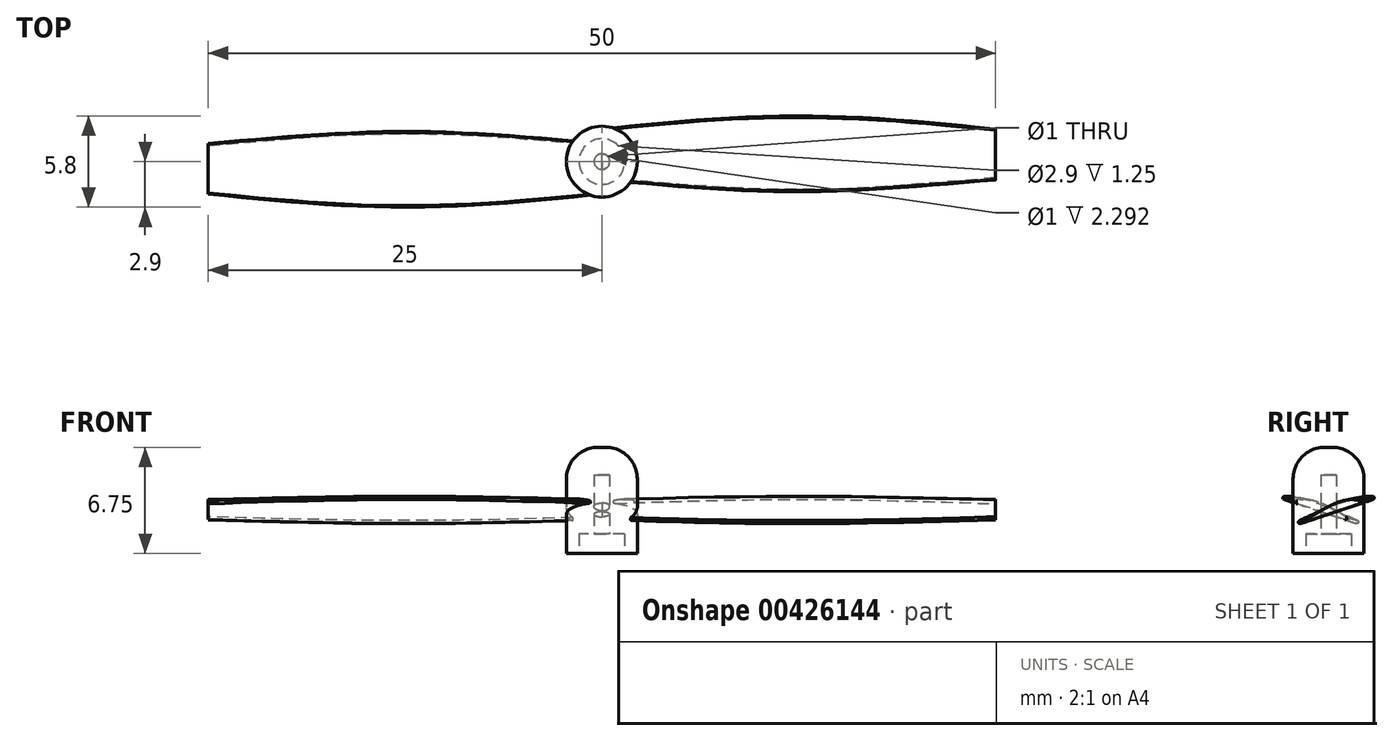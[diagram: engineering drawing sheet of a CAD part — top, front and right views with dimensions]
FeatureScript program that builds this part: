
annotation { "Feature Type Name" : "Feature", "Feature Type Description" : "" }
export const myFeature = defineFeature(function(context is Context, id is Id, definition is map)
    precondition{}
    {
        {
            var Q0;
            Q0=qCreatedBy(makeId("Top.planeOp"),FACE);
            var sketch = newSketch(context, id + "F0", { "sketchPlane" : qUnion([Q0])});
            skCircle(sketch, "E0", {"center": v(0, 0) * mm, "radius": 2.25 * mm});
            skCircle(sketch, "E1", {"center": v(0, 0) * mm, "radius": 1.45 * mm});
            skCircle(sketch, "E2", {"center": v(0, 0) * mm, "radius": 0.5 * mm});
            skSolve(sketch);
        }
        {
            var Q0;
            Q0=makeQuery(id+"F0.imprint","IMPRINT",FACE,{"disambiguationData":[TD([[makeQuery(id+"F0.imprint","IMPRINT",EDGE,{"derivedFrom":sQuery(id+"F0.wireOp",EDGE,"E0")}),1.0]])]});
            extrude(context, id + "F1", {"entities" : qUnion([Q0]), "depth" : 6.75 * mm, "offsetDistance" : 25 * mm});
        }
        {
            var Q0;
            Q0=makeQuery(id+"F0.imprint","IMPRINT",FACE,{"disambiguationData":[TD([[makeQuery(id+"F0.imprint","IMPRINT",EDGE,{"derivedFrom":sQuery(id+"F0.wireOp",EDGE,"E1")}),1.0]])]});
            extrude(context, id + "F2", {"entities" : qUnion([Q0]), "operationType" : NewBodyOperationType.ADD, "depth" : 6.75 * mm, "offsetDistance" : 25 * mm, "hasSecondDirection" : true, "secondDirectionOppositeDirection" : false, "secondDirectionDepth" : 1.25 * mm});
        }
        {
            var Q0;
            Q0=makeQuery(id+"F0.imprint","IMPRINT",FACE,{"disambiguationData":[TD([[makeQuery(id+"F0.imprint","IMPRINT",EDGE,{"derivedFrom":sQuery(id+"F0.wireOp",EDGE,"E2")}),1.0]])]});
            extrude(context, id + "F3", {"entities" : qUnion([Q0]), "operationType" : NewBodyOperationType.ADD, "depth" : 6.75 * mm, "offsetDistance" : 25 * mm, "hasSecondDirection" : true, "secondDirectionOppositeDirection" : false, "secondDirectionDepth" : 5 * mm});
        }
        {
            var Q0;
            Q0=makeQuery(id+"F1.opExtrude","CAP_EDGE",EDGE,{"disambiguationData":[OSD([sQuery(id+"F0.wireOp",EDGE,"E0")])],"isStart":false});
            fillet(context, id + "F4", {"entities" : qUnion([Q0]), "radius" : 2 * mm, "tangentPropagation" : true, "allowEdgeOverflow" : false});
        }
        {
            var Q0;
            Q0=qCreatedBy(makeId("Right.planeOp"),FACE);
            var sketch = newSketch(context, id + "F5", { "sketchPlane" : qUnion([Q0])});
            skLineSegment(sketch, "E3", {"start": v(2.25, 3.25) * mm, "end": v(-2.25, 1.75) * mm});
            skFitSpline(sketch, "E4", {"points": [v(2.25, 3.25) * mm, v(-2.25, 1.75) * mm], "startDerivative": vector(-4.5, 2.25) * mm, "endDerivative": vector(-3.75, -1.25) * mm});
            skSolve(sketch);
        }
        {
            var Q0;
            Q0=qCreatedBy(makeId("Right.planeOp"),FACE);
            cPlane(context, id + "F6", {"entities" : qUnion([Q0]), "cplaneType" : CPlaneType.OFFSET, "offset" : 12 * mm, "width" : 150 * mm, "height" : 150 * mm});
        }
        {
            var Q0;
            Q0=qCreatedBy(id+"F6.planeOp",FACE);
            var sketch = newSketch(context, id + "F7", { "sketchPlane" : qUnion([Q0])});
            skLineSegment(sketch, "E5", {"start": v(-3.88, 1.2) * mm, "end": v(3.24, 3.58) * mm});
            skFitSpline(sketch, "E6", {"points": [v(-3.88, 1.2) * mm, v(3.24, 3.58) * mm], "startDerivative": vector(7.12, 2.73) * mm, "endDerivative": vector(5.22, -1.26) * mm});
            skSolve(sketch);
        }
        {
            var Q0;
            Q0=qCreatedBy(makeId("Right.planeOp"),FACE);
            cPlane(context, id + "F8", {"entities" : qUnion([Q0]), "cplaneType" : CPlaneType.OFFSET, "offset" : 25 * mm, "width" : 150 * mm, "height" : 150 * mm});
        }
        {
            var Q0;
            Q0=qCreatedBy(id+"F8.planeOp",FACE);
            var sketch = newSketch(context, id + "F9", { "sketchPlane" : qUnion([Q0])});
            skLineSegment(sketch, "E7", {"start": v(-2.25, 1.75) * mm, "end": v(2.25, 3.25) * mm});
            skFitSpline(sketch, "E8", {"points": [v(-2.25, 1.75) * mm, v(2.25, 3.25) * mm], "startDerivative": vector(3.75, 1.25) * mm, "endDerivative": vector(4.5, -2.25) * mm});
            skSolve(sketch);
        }
        {
            var Q1;
            Q1=makeQuery(id+"F5.imprint","IMPRINT",FACE,{"disambiguationData":[TD([[makeQuery(id+"F5.imprint","IMPRINT",EDGE,{"derivedFrom":sQuery(id+"F5.wireOp",EDGE,"E3")}),-1.0]])]});
            var Q2;
            Q2=makeQuery(id+"F7.imprint","IMPRINT",FACE,{"disambiguationData":[TD([[makeQuery(id+"F7.imprint","IMPRINT",EDGE,{"derivedFrom":sQuery(id+"F7.wireOp",EDGE,"E5")}),1.0]])]});
            var Q3;
            Q3=makeQuery(id+"F9.imprint","IMPRINT",FACE,{"disambiguationData":[TD([[makeQuery(id+"F9.imprint","IMPRINT",EDGE,{"derivedFrom":sQuery(id+"F9.wireOp",EDGE,"E7")}),1.0]])]});
            loft(context, id + "F10", {"sheetProfilesArray" : [{ "sheetProfileEntities" : qUnion([Q1]) }, { "sheetProfileEntities" : qUnion([Q2]) }, { "sheetProfileEntities" : qUnion([Q3]) }]});
        }
        {
            var Q0;
            {var subQ0=sQuery(id+"F7.wireOp",EDGE,"E6");var subQ1=sQuery(id+"F7.wireOp",EDGE,"E5");var subQ2=sQuery(id+"F5.wireOp",EDGE,"E4");var subQ3=sQuery(id+"F5.wireOp",EDGE,"E3");Q0=makeQuery(id+"F10.opLoft","SWEPT_EDGE",EDGE,{"disambiguationData":[OSD([subQ3,subQ2,subQ1,subQ0]),TDD([makeQuery(id+"F5.imprint","INTERSECT",VERTEX,{"disambiguationData":[OD(1.0)],"derivedFrom":[subQ3,subQ2]}),makeQuery(id+"F7.imprint","INTERSECT",VERTEX,{"disambiguationData":[OD(0.0)],"derivedFrom":[subQ1,subQ0]})])]});}
            var Q1;
            {var subQ0=sQuery(id+"F7.wireOp",EDGE,"E6");var subQ1=sQuery(id+"F7.wireOp",EDGE,"E5");var subQ2=sQuery(id+"F5.wireOp",EDGE,"E4");var subQ3=sQuery(id+"F5.wireOp",EDGE,"E3");Q1=makeQuery(id+"F10.opLoft","SWEPT_EDGE",EDGE,{"disambiguationData":[OSD([subQ3,subQ2,subQ1,subQ0]),TDD([makeQuery(id+"F5.imprint","INTERSECT",VERTEX,{"disambiguationData":[OD(0.0)],"derivedFrom":[subQ3,subQ2]}),makeQuery(id+"F7.imprint","INTERSECT",VERTEX,{"disambiguationData":[OD(1.0)],"derivedFrom":[subQ1,subQ0]})])]});}
            fillet(context, id + "F11", {"entities" : qUnion([Q0, Q1]), "radius" : .1 * mm, "tangentPropagation" : true, "allowEdgeOverflow" : false});
        }
        {
            var Q0;
            Q0=makeQuery(id+"F10.opLoft","SWEPT_BODY",BODY,{"disambiguationData":[OSD([makeQuery(id+"F5.imprint","IMPRINT",FACE,{"disambiguationData":[TD([[makeQuery(id+"F5.imprint","IMPRINT",EDGE,{"derivedFrom":sQuery(id+"F5.wireOp",EDGE,"E3")}),-1.0]])]}),sQuery(id+"F7.wireOp",EDGE,"E6"),makeQuery(id+"F9.imprint","IMPRINT",FACE,{"disambiguationData":[TD([[makeQuery(id+"F9.imprint","IMPRINT",EDGE,{"derivedFrom":sQuery(id+"F9.wireOp",EDGE,"E7")}),1.0]])]})])]});
            var Q1;
            Q1=sQuery(id+"F0.wireOp",EDGE,"E0");
            circularPattern(context, id + "F12", {"operationType" : NewBodyOperationType.ADD, "entities" : qUnion([Q0]), "axis" : qUnion([Q1]), "angle" : 360 * degree, "instanceCount" : 2, "equalSpace" : true});
        }
    });
